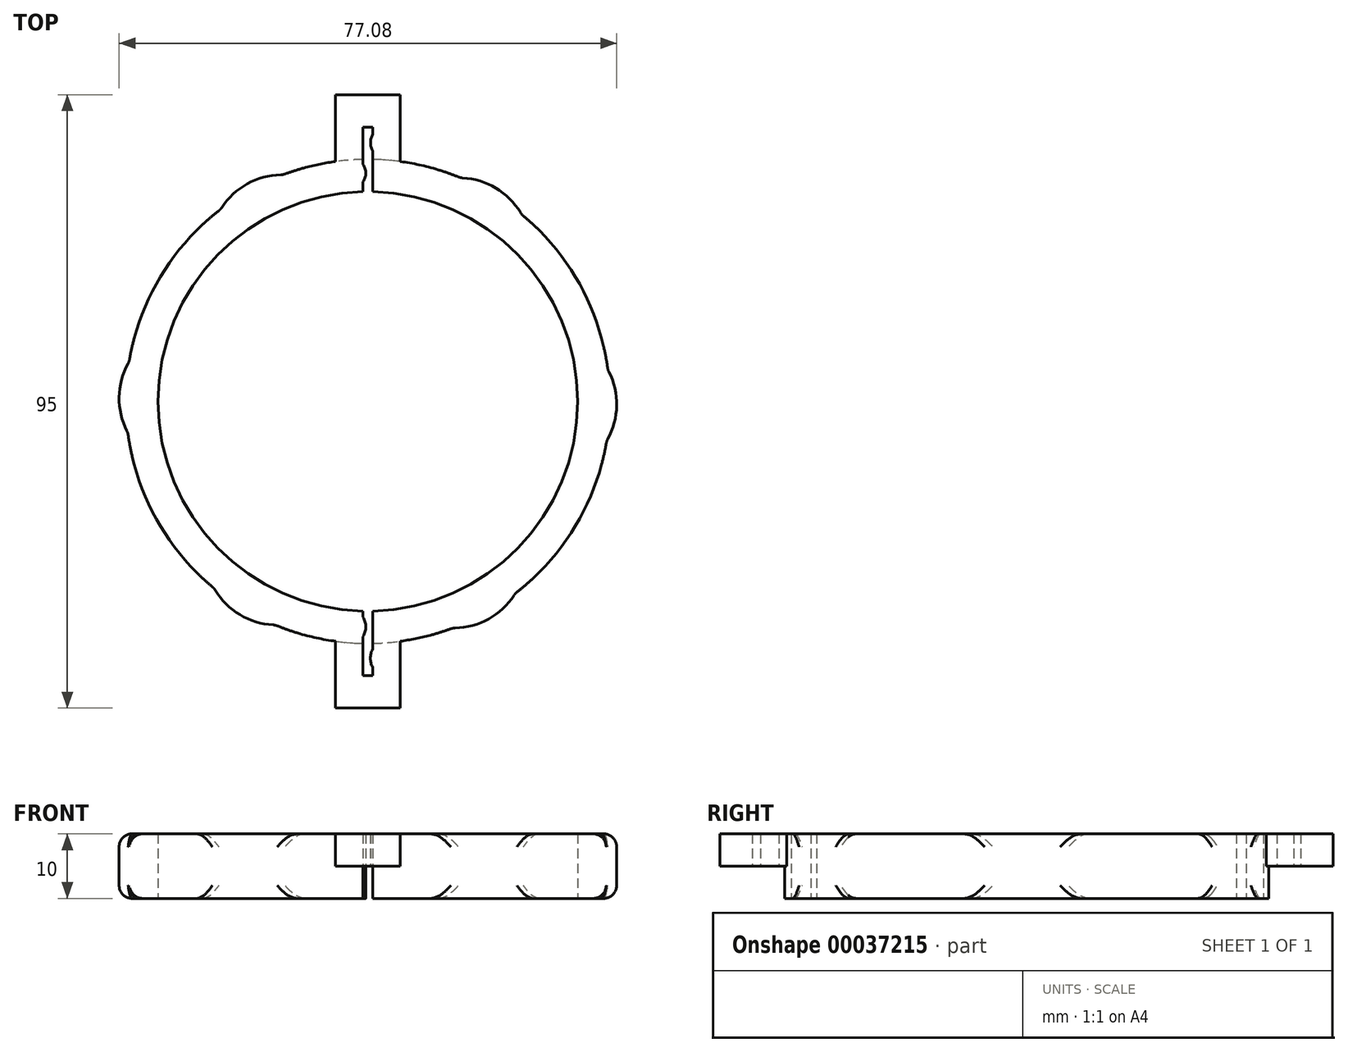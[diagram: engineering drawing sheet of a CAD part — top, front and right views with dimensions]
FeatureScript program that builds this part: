
annotation { "Feature Type Name" : "Feature", "Feature Type Description" : "" }
export const myFeature = defineFeature(function(context is Context, id is Id, definition is map)
    precondition{}
    {
        {
            var Q0;
            Q0=qCreatedBy(makeId("Top.planeOp"),FACE);
            var sketch = newSketch(context, id + "F0", { "sketchPlane" : qUnion([Q0])});
            skCircle(sketch, "E0", {"center": v(0, 0) * mm, "radius": 37.5 * mm});
            skCircle(sketch, "E1", {"center": v(0, 0) * mm, "radius": 32.5 * mm});
            skLineSegment(sketch, "E2.rect.bottom", {"start": v(-5, 47.5) * mm, "end": v(5, 47.5) * mm});
            skLineSegment(sketch, "E2.rect.top", {"start": v(-5, -47.5) * mm, "end": v(5, -47.5) * mm});
            skLineSegment(sketch, "E2.rect.left", {"start": v(-5, 47.5) * mm, "end": v(-5, -47.5) * mm});
            skLineSegment(sketch, "E2.rect.right", {"start": v(5, 47.5) * mm, "end": v(5, -47.5) * mm});
            skLineSegment(sketch, "E3.rect.bottom", {"start": v(-0.75, 42.5) * mm, "end": v(0.75, 42.5) * mm});
            skLineSegment(sketch, "E3.rect.top", {"start": v(-0.75, -42.5) * mm, "end": v(0.75, -42.5) * mm});
            skLineSegment(sketch, "E3.rect.left", {"start": v(-0.75, 42.5) * mm, "end": v(-0.75, 36.7) * mm});
            skLineSegment(sketch, "E3.rect.right", {"start": v(0.75, 42.5) * mm, "end": v(0.75, 41.38) * mm});
            skArc(sketch, "E4", {"start": v(0.75, 41.38) * mm, "mid": v(0.4, 40.08) * mm, "end": v(0.75, 38.77) * mm});
            skArc(sketch, "E5", {"start": v(-0.75, 34.03) * mm, "mid": v(-0.33, 35.37) * mm, "end": v(-0.75, 36.7) * mm});
            skArc(sketch, "E6", {"start": v(0.75, -38.38) * mm, "mid": v(0.39, -39.8) * mm, "end": v(0.75, -41.22) * mm});
            skArc(sketch, "E7", {"start": v(-0.75, -36.45) * mm, "mid": v(-0.32, -34.92) * mm, "end": v(-0.75, -33.4) * mm});
            skLineSegment(sketch, "E8", {"start": v(-0.75, -36.45) * mm, "end": v(-0.75, -42.5) * mm});
            skLineSegment(sketch, "E9", {"start": v(0.75, -41.22) * mm, "end": v(0.75, -42.5) * mm});
            skLineSegment(sketch, "E10", {"start": v(-0.75, 34.03) * mm, "end": v(-0.75, -33.4) * mm});
            skLineSegment(sketch, "E11", {"start": v(0.75, 38.77) * mm, "end": v(0.75, -38.38) * mm});
            skArc(sketch, "E12", {"start": v(-37, 6.14) * mm, "mid": v(-38.54, 0.65) * mm, "end": v(-37.18, -4.88) * mm});
            skArc(sketch, "E13.1.0", {"start": v(-23.82, -28.96) * mm, "mid": v(-19.84, -33.05) * mm, "end": v(-14.36, -34.64) * mm});
            skArc(sketch, "E13.2.0", {"start": v(13.18, -35.1) * mm, "mid": v(18.7, -33.7) * mm, "end": v(22.82, -29.76) * mm});
            skArc(sketch, "E13.3.0", {"start": v(37, -6.14) * mm, "mid": v(38.54, -0.65) * mm, "end": v(37.18, 4.88) * mm});
            skArc(sketch, "E13.4.0", {"start": v(23.82, 28.96) * mm, "mid": v(19.84, 33.05) * mm, "end": v(14.36, 34.64) * mm});
            skArc(sketch, "E13.5.0", {"start": v(-13.18, 35.1) * mm, "mid": v(-18.7, 33.7) * mm, "end": v(-22.82, 29.76) * mm});
            skSolve(sketch);
        }
        {
            var Q0;
            Q0 = qSketchRegion(id + "F0", true);
            extrude(context, id + "F1", {"entities" : qUnion([Q0]), "depth" : 10 * mm});
        }
        {
            var Q0;
            {var subQ8=sQuery(id+"F0.wireOp",EDGE,"E2.rect.bottom");Q0=makeQuery(id+"F0.imprint","IMPRINT",FACE,{"disambiguationData":[TD([[makeQuery(id+"F0.imprint","IMPRINT",EDGE,{"derivedFrom":subQ8}),-1.0]])]});}
            var Q1;
            {var subQ8=sQuery(id+"F0.wireOp",EDGE,"E2.rect.top");Q1=makeQuery(id+"F0.imprint","IMPRINT",FACE,{"disambiguationData":[TD([[makeQuery(id+"F0.imprint","IMPRINT",EDGE,{"derivedFrom":subQ8}),1.0]])]});}
            extrude(context, id + "F2", {"entities" : qUnion([Q0, Q1]), "operationType" : NewBodyOperationType.REMOVE, "depth" : 5 * mm});
        }
        {
            var Q0;
            Q0=sQuery(id+"F0.wireOp",EDGE,"E7");
            var Q1;
            Q1=sQuery(id+"F0.wireOp",EDGE,"E5");
            extrude(context, id + "F3", {"bodyType" : ToolBodyType.SURFACE, "surfaceEntities" : qUnion([Q0, Q1]), "depth" : 10 * mm});
        }
        {
            var Q0;
            Q0=sQuery(id+"F0.wireOp",EDGE,"E4");
            var Q1;
            Q1=sQuery(id+"F0.wireOp",EDGE,"E5");
            extrude(context, id + "F4", {"bodyType" : ToolBodyType.SURFACE, "surfaceEntities" : qUnion([Q0, Q1]), "depth" : 10 * mm, "hasSecondDirection" : true, "secondDirectionOppositeDirection" : false, "secondDirectionDepth" : 5 * mm});
        }
        {
            var Q0;
            Q0=makeQuery(id+"F1.opExtrude","SWEPT_FACE",FACE,{"disambiguationData":[OSD([sQuery(id+"F0.wireOp",EDGE,"E3.rect.left")])]});
            extrude(context, id + "F5", {"entities" : qUnion([Q0]), "operationType" : NewBodyOperationType.ADD, "endBound" : BoundingType.UP_TO_NEXT, "oppositeDirection" : true, "depth" : 5.58 * mm});
        }
        {
            var Q0;
            Q0=makeQuery(id+"F1.opExtrude","SWEPT_FACE",FACE,{"disambiguationData":[OSD([sQuery(id+"F0.wireOp",EDGE,"E12")])]});
            var Q1;
            Q1=makeQuery(id+"F1.opExtrude","SWEPT_FACE",FACE,{"disambiguationData":[OSD([sQuery(id+"F0.wireOp",EDGE,"E13.1.0")])]});
            var Q2;
            Q2=makeQuery(id+"F1.opExtrude","SWEPT_FACE",FACE,{"disambiguationData":[OSD([sQuery(id+"F0.wireOp",EDGE,"E13.5.0")])]});
            var Q3;
            Q3=makeQuery(id+"F1.opExtrude","SWEPT_FACE",FACE,{"disambiguationData":[OSD([sQuery(id+"F0.wireOp",EDGE,"E13.4.0")])]});
            var Q4;
            Q4=makeQuery(id+"F1.opExtrude","SWEPT_FACE",FACE,{"disambiguationData":[OSD([sQuery(id+"F0.wireOp",EDGE,"E13.3.0")])]});
            var Q5;
            Q5=makeQuery(id+"F1.opExtrude","SWEPT_FACE",FACE,{"disambiguationData":[OSD([sQuery(id+"F0.wireOp",EDGE,"E13.2.0")])]});
            fillet(context, id + "F6", {"entities" : qUnion([Q0, Q1, Q2, Q3, Q4, Q5]), "radius" : 2 * mm, "tangentPropagation" : true, "allowEdgeOverflow" : false});
        }
    });
